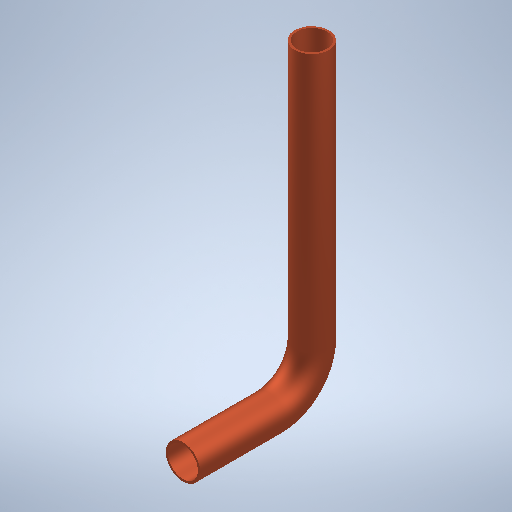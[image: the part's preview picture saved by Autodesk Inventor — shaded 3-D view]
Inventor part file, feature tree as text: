
AUTODESK INVENTOR PART (.ipt)
format: ipt  version: 2025 (Build 290162010, 162A)  size: 277,504 bytes
history: native  units: mm
features: sketch x2, plane x1, sweep x1
ambient origin geometry x8: Origin, YZ Plane, XZ Plane, XY Plane, X Axis, Y Axis, Z Axis, Center Point
bodies: Volumenkörper1 (feature_tree)
feature tree (4):
  sketch  "Skizze1"  dims[d0=8.0mm d1=7.0mm]
  plane  "Arbeitsebene1"
  sweep  "Sweeping1"
  sketch  "Skizze2"  dims[d2=0.0mm d3=70.0mm d4=10.0mm d5=30.0mm d6=0.0mm d7=0.0mm]
